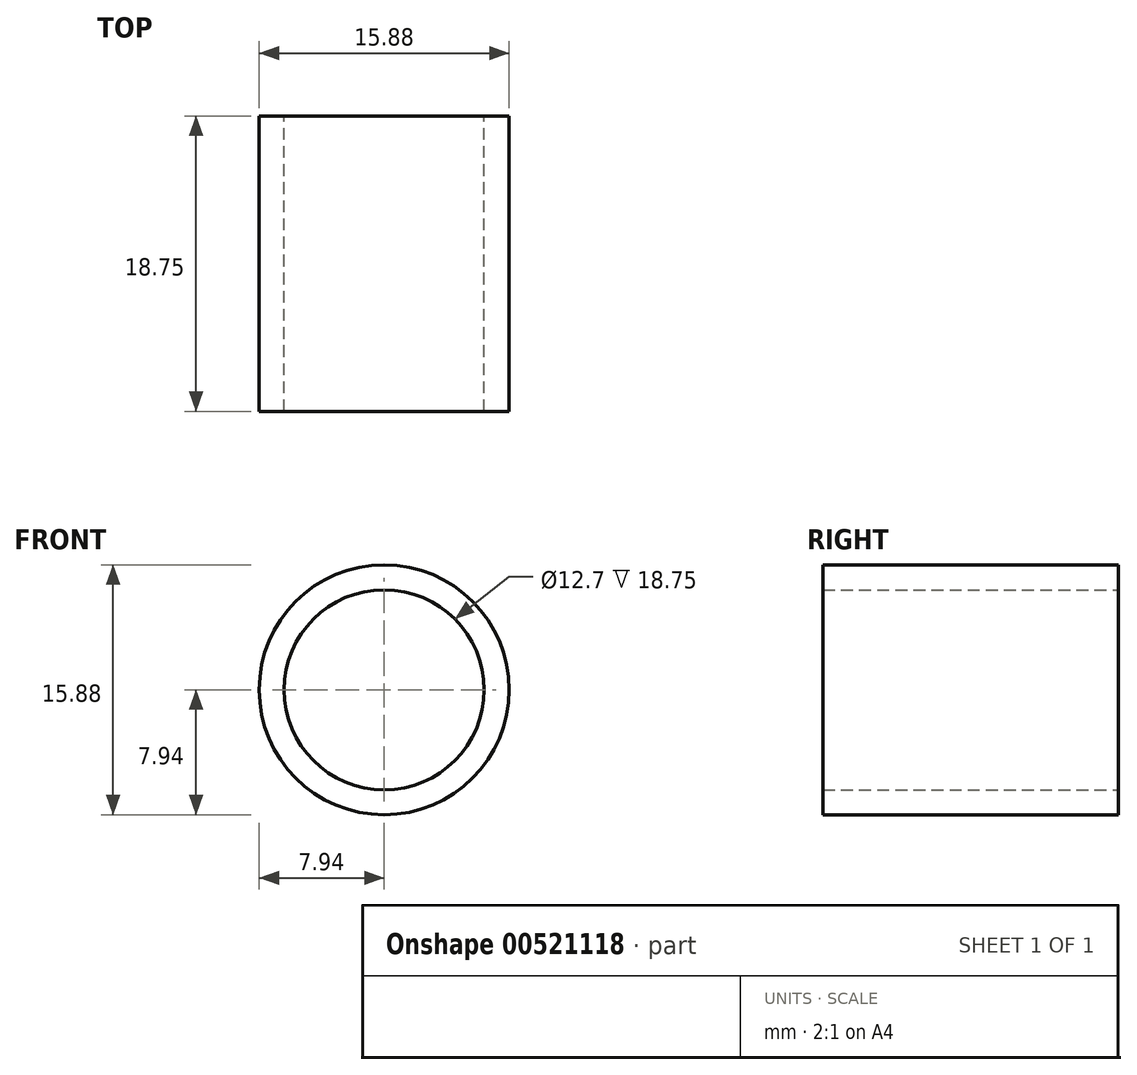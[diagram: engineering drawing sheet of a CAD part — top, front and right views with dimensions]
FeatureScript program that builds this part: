
annotation { "Feature Type Name" : "Feature", "Feature Type Description" : "" }
export const myFeature = defineFeature(function(context is Context, id is Id, definition is map)
    precondition{}
    {
        {
            var Q0;
            Q0=qCreatedBy(makeId("Front.planeOp"),FACE);
            var sketch = newSketch(context, id + "F0", { "sketchPlane" : qUnion([Q0])});
            skCircle(sketch, "E0", {"center": v(0, 0) * mm, "radius": 6.35 * mm});
            skCircle(sketch, "E1", {"center": v(0, 0) * mm, "radius": 7.94 * mm});
            skSolve(sketch);
        }
        {
            assignVariable(context, id + "F1", {"name" : "Tube_Length", "anyValue" : 18.75});
        }
        {
            var Q0;
            Q0=makeQuery(id+"F0.imprint","IMPRINT",FACE,{"disambiguationData":[TD([[makeQuery(id+"F0.imprint","IMPRINT",EDGE,{"derivedFrom":sQuery(id+"F0.wireOp",EDGE,"E0")}),-1.0]])]});
            extrude(context, id + "F2", {"entities" : qUnion([Q0]), "depth" : (getVariable(context, 'Tube_Length')) * mm, "offsetDistance" : 25.4 * mm});
        }
    });
